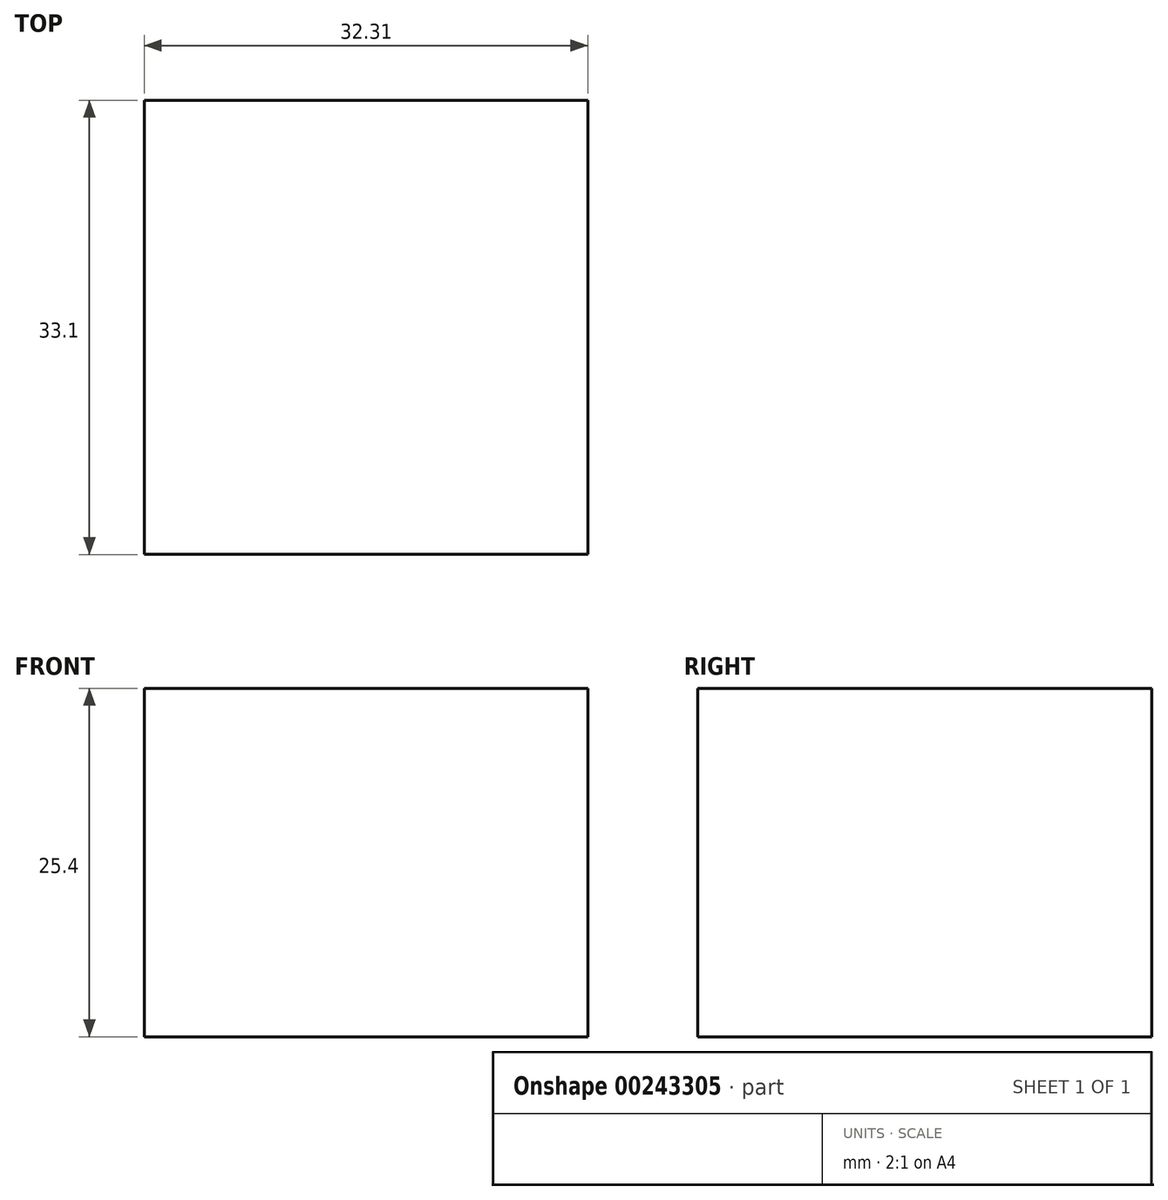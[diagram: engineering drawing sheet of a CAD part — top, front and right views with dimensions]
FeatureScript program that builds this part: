
annotation { "Feature Type Name" : "Feature", "Feature Type Description" : "" }
export const myFeature = defineFeature(function(context is Context, id is Id, definition is map)
    precondition{}
    {
        {
            var Q0;
            Q0=qCreatedBy(makeId("Top.planeOp"),FACE);
            var sketch = newSketch(context, id + "F0", { "sketchPlane" : qUnion([Q0])});
            skLineSegment(sketch, "E0.bottom", {"start": v(0, 0) * mm, "end": v(32.31, 0) * mm});
            skLineSegment(sketch, "E0.top", {"start": v(0, -33.1) * mm, "end": v(32.31, -33.1) * mm});
            skLineSegment(sketch, "E0.left", {"start": v(0, 0) * mm, "end": v(0, -33.1) * mm});
            skLineSegment(sketch, "E0.right", {"start": v(32.31, 0) * mm, "end": v(32.31, -33.1) * mm});
            skSolve(sketch);
        }
        {
            var Q0;
            Q0=makeQuery(id+"F0.imprint","IMPRINT",FACE,{"disambiguationData":[TD([[makeQuery(id+"F0.imprint","IMPRINT",EDGE,{"derivedFrom":sQuery(id+"F0.wireOp",EDGE,"E0.bottom")}),-1.0]])]});
            extrude(context, id + "F1", {"entities" : qUnion([Q0]), "depth" : 25.4 * mm});
        }
    });
